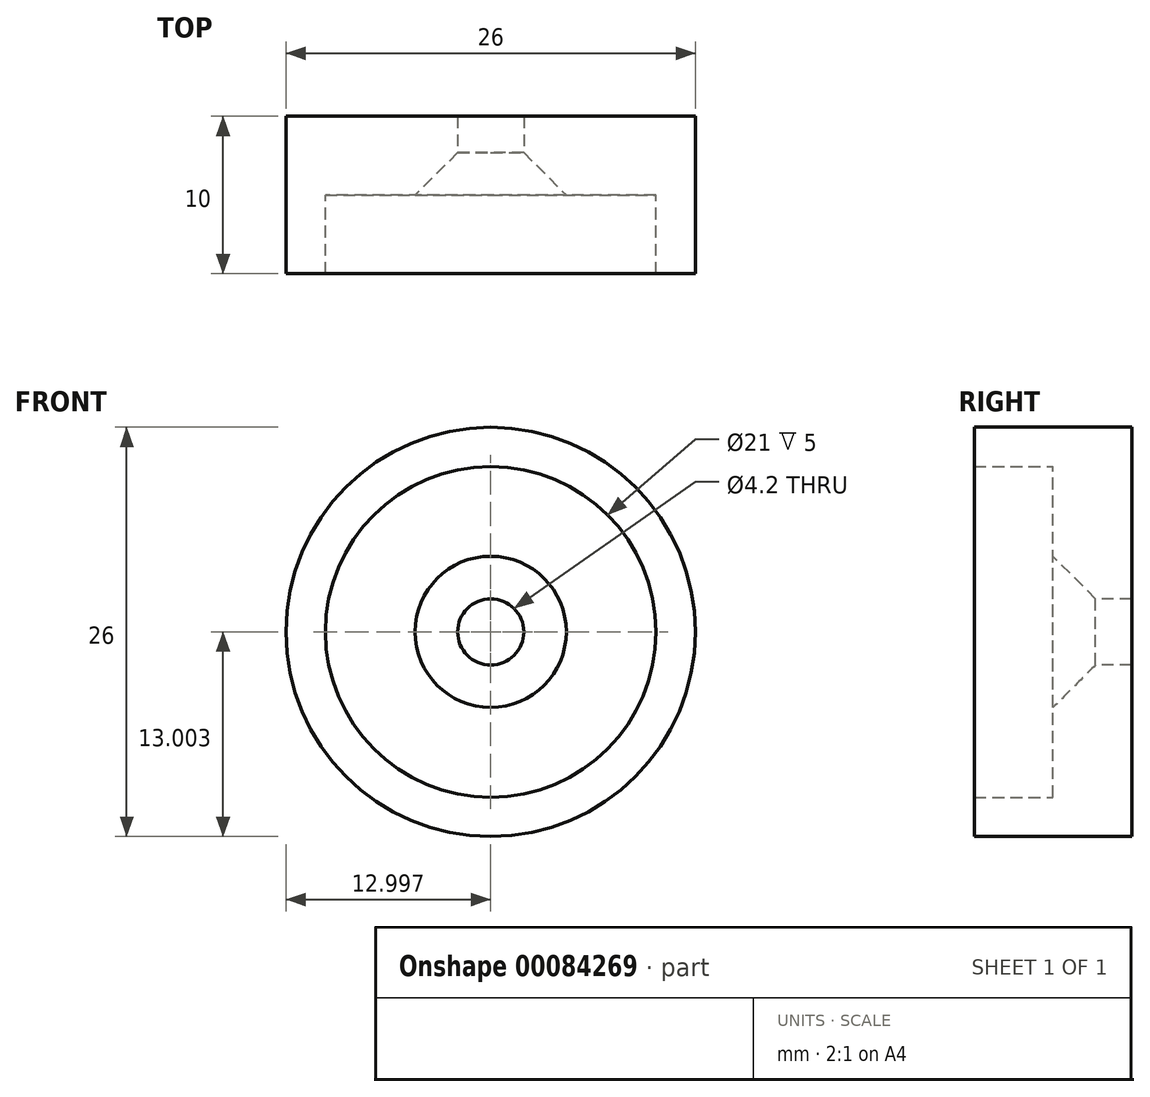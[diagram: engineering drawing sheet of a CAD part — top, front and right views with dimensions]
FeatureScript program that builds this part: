
annotation { "Feature Type Name" : "Feature", "Feature Type Description" : "" }
export const myFeature = defineFeature(function(context is Context, id is Id, definition is map)
    precondition{}
    {
        {
            var Q0;
            Q0=qCreatedBy(makeId("Front.planeOp"),FACE);
            var sketch = newSketch(context, id + "F0", { "sketchPlane" : qUnion([Q0])});
            skCircle(sketch, "E0", {"center": v(-16.95, -2.17) * mm, "radius": 10.5 * mm});
            skCircle(sketch, "E1", {"center": v(-16.95, -2.17) * mm, "radius": 13 * mm});
            skCircle(sketch, "E2", {"center": v(-16.95, -2.17) * mm, "radius": 2.1 * mm});
            skSolve(sketch);
        }
        {
            var Q0;
            Q0=makeQuery(id+"F0.imprint","IMPRINT",FACE,{"disambiguationData":[TD([[makeQuery(id+"F0.imprint","IMPRINT",EDGE,{"derivedFrom":sQuery(id+"F0.wireOp",EDGE,"E0")}),-1.0]])]});
            extrude(context, id + "F1", {"entities" : qUnion([Q0]), "depth" : 5 * mm});
        }
        {
            var Q0;
            Q0=makeQuery(id+"F0.imprint","IMPRINT",FACE,{"disambiguationData":[TD([[makeQuery(id+"F0.imprint","IMPRINT",EDGE,{"derivedFrom":sQuery(id+"F0.wireOp",EDGE,"E0")}),1.0]])]});
            var Q1;
            Q1=makeQuery(id+"F0.imprint","IMPRINT",FACE,{"disambiguationData":[TD([[makeQuery(id+"F0.imprint","IMPRINT",EDGE,{"derivedFrom":sQuery(id+"F0.wireOp",EDGE,"E0")}),-1.0]])]});
            extrude(context, id + "F2", {"entities" : qUnion([Q0, Q1]), "operationType" : NewBodyOperationType.ADD, "oppositeDirection" : true, "depth" : 5 * mm});
        }
        {
            var Q0;
            Q0=makeQuery(id+"F2.opExtrude","CAP_EDGE",EDGE,{"disambiguationData":[OSD([sQuery(id+"F0.wireOp",EDGE,"E2")])],"isStart":true});
            chamfer(context, id + "F3", {"entities" : qUnion([Q0]), "chamferType" : ChamferType.OFFSET_ANGLE, "width" : 2.7 * mm, "oppositeDirection" : false, "angle" : 45 * degree, "tangentPropagation" : true});
        }
    });
